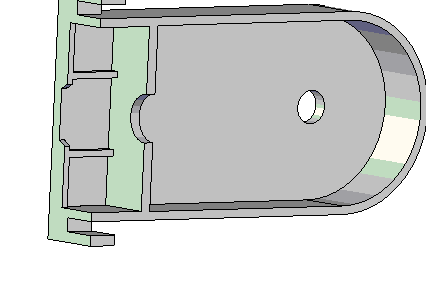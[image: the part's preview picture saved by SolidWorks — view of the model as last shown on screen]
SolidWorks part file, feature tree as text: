
SOLIDWORKS PART (.sldprt)
format: sldprt  version: not decoded by parser v0  size: 361,984 bytes
history: native  units: mm
features: sketch x10, cut_extrude x7, extrude x3 (+10 scaffold rows collapsed)
feature tree (30):
  scaffold x10  (default folders/planes/origin — collapsed)
  sketch  "Sketch1"  dims[c1.D1=19.9644mm c1.D4=19.9644mm c2.D1=2.286mm c2.D2=2.9718mm c2.D3=2.413mm c2.D4=40.767mm c2.D5=9.9822mm]
  extrude  "Extrude1"  Depth=6.858mm
  sketch  "Sketch2"  dims[c1.D1=~1.497873mm c1.D3=3.0226mm c1.D4=3.0226mm c1.D5=3.0226mm c1.D6=5.1816mm c1.D7=2.032mm c1.D8=3.0226mm c2.D7=5.1562mm c2.D2=3.0226mm c2.D1=21.844mm c3.D2=13.6652mm c3.D3=8.382mm c3.D8=17.1196mm c3.D9=40.767mm c3.D7=30.7848mm]
  sketch  "Sketch6"  dims[c1.D1=3.048mm c1.D2=3.048mm c1.D3=3.048mm c2.D1=13.589mm]
  extrude  "Extrude2"  Depth=0.508mm
  extrude  "Extrude3"  Depth=0.254mm
  sketch  "Sketch7"  dims[D1=3.302mm]
  cut_extrude  "Cut-Extrude1"  [1 undecoded]
  sketch  "Sketch8"  dims[D1=1.3716mm D2=3.048mm]
  cut_extrude  "Cut-Extrude2"  [1 undecoded]
  sketch  "Sketch10"  dims[c1.D1=4.826mm c1.D2=0.889mm c1.D3=9.9822mm c1.D4=4.826mm c2.D1=4.826mm c2.D2=0.889mm c2.D3=0.889mm]
  cut_extrude  "Cut-Extrude3"  Depth=6.0706mm
  sketch  "Sketch11"  dims[c1.D1=5.334mm c1.D2=0.635mm c1.D3=0.127mm c2.D2=0.635mm c2.D1=4.9276mm c2.D3=0.635mm c2.D4=0.635mm]
  cut_extrude  "Cut-Extrude4"  Depth=0.9144mm
  sketch  "Sketch12"  dims[D1=2.54mm D2=3.048mm]
  cut_extrude  "Cut-Extrude10"  [1 undecoded]
  sketch  "Sketch15"  dims[D1=1.016mm]
  cut_extrude  "Cut-Extrude15"  [1 undecoded]
  sketch  "Sketch16"  dims[D1=~2.79016mm]
  cut_extrude  "Cut-Extrude16"  [1 undecoded]
decode coverage: 15 of 20 modeling features carry decoded parameters
note: ~ marks probable driven/reference dimensions
note: 5 parameter values undecoded
summary: no parameter record found for 5 features
note: suppression state not decoded; provenance and decode notes live in map.json
